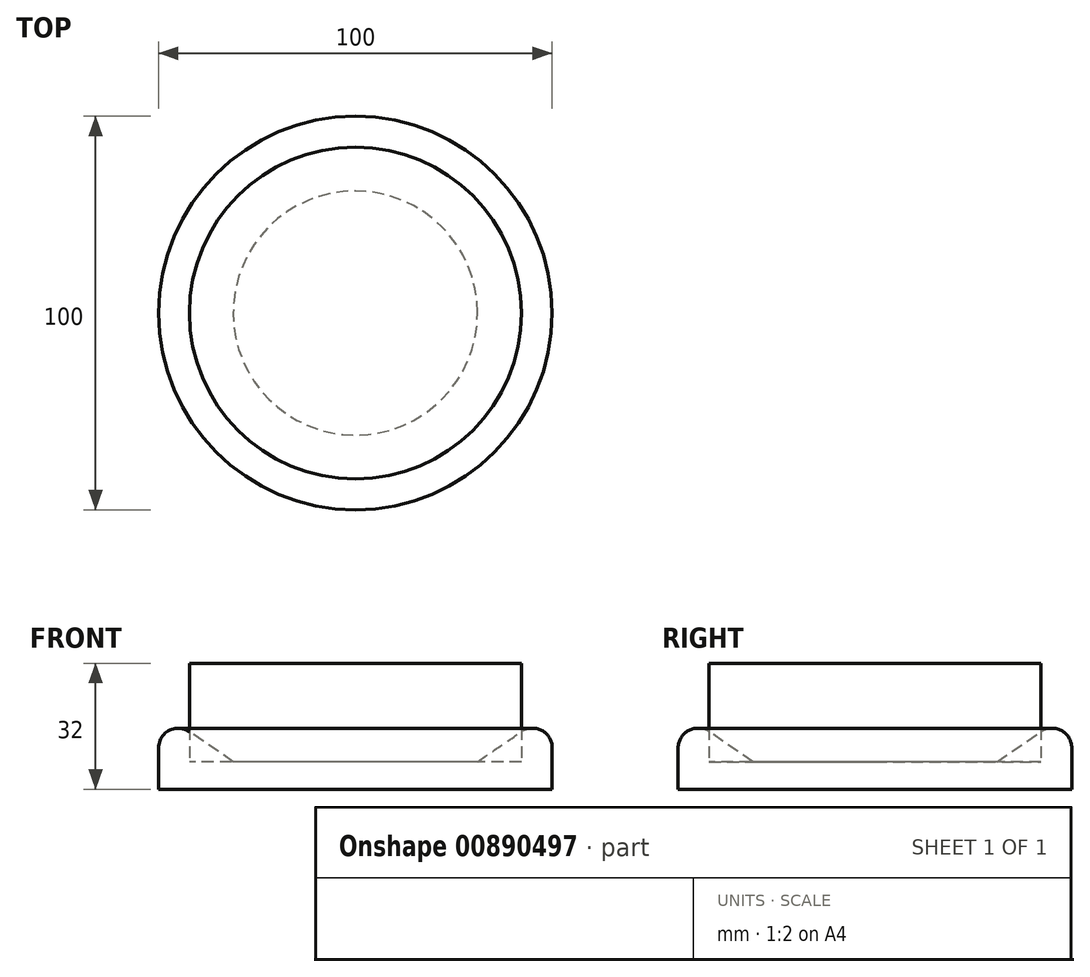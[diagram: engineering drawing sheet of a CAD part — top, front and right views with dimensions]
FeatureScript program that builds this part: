
annotation { "Feature Type Name" : "Feature", "Feature Type Description" : "" }
export const myFeature = defineFeature(function(context is Context, id is Id, definition is map)
    precondition{}
    {
        {
            var Q0;
            Q0=qCreatedBy(makeId("Front.planeOp"),FACE);
            var sketch = newSketch(context, id + "F0", { "sketchPlane" : qUnion([Q0])});
            skLineSegment(sketch, "E0", {"start": v(0, 0) * mm, "end": v(-50, 0) * mm});
            skLineSegment(sketch, "E1", {"start": v(-50, 0) * mm, "end": v(-50, 20) * mm});
            skLineSegment(sketch, "E2", {"start": v(-50, 20) * mm, "end": v(-31.03, 7) * mm});
            skLineSegment(sketch, "E3", {"start": v(-31.03, 7) * mm, "end": v(0, 7) * mm});
            skLineSegment(sketch, "E4", {"start": v(0, 7) * mm, "end": v(0, 0) * mm});
            skSolve(sketch);
        }
        {
            var Q0;
            Q0 = qSketchRegion(id + "F0", true);
            var Q1;
            Q1=sQuery(id+"F0.wireOp",EDGE,"E4");
            revolve(context, id + "F1", {"surfaceOperationType" : NewSurfaceOperationType.NEW, "entities" : qUnion([Q0]), "axis" : qUnion([Q1]), "revolveType" : RevolveType.FULL});
        }
        {
            var Q0;
            Q0=makeQuery(id+"F1.opRevolve","SWEPT_EDGE",EDGE,{"disambiguationData":[OSD([sQuery(id+"F0.wireOp",EDGE,"E1"),sQuery(id+"F0.wireOp",EDGE,"E2")])]});
            fillet(context, id + "F2", {"entities" : qUnion([Q0]), "radius" : 5 * mm, "tangentPropagation" : true, "allowEdgeOverflow" : false});
        }
        {
            var Q0;
            Q0=makeQuery(id+"F1.opRevolve","SWEPT_FACE",FACE,{"disambiguationData":[OSD([sQuery(id+"F0.wireOp",EDGE,"E3")])]});
            var sketch = newSketch(context, id + "F3", { "sketchPlane" : qUnion([Q0])});
            skCircle(sketch, "E5.0", {"center": v(0, 0) * mm, "radius": 42.17 * mm});
            skCircle(sketch, "E5.1", {"center": v(0, 0) * mm, "radius": 31.03 * mm});
            skSolve(sketch);
        }
        {
            var Q0;
            Q0=makeQuery(id+"F3.imprint","IMPRINT",FACE,{"disambiguationData":[TD([[makeQuery(id+"F3.imprint","IMPRINT",EDGE,{"derivedFrom":sQuery(id+"F3.wireOp",EDGE,"E5.1")}),1.0]])]});
            var Q1;
            Q1=makeQuery(id+"F3.imprint","IMPRINT",FACE,{"disambiguationData":[TD([[makeQuery(id+"F3.imprint","IMPRINT",EDGE,{"derivedFrom":sQuery(id+"F3.wireOp",EDGE,"E5.0")}),1.0]])]});
            extrude(context, id + "F4", {"entities" : qUnion([Q0, Q1]), "depth" : 25 * mm, "offsetDistance" : 25 * mm});
        }
    });
